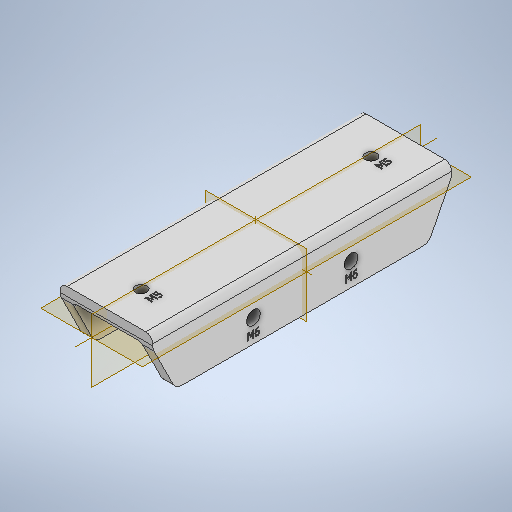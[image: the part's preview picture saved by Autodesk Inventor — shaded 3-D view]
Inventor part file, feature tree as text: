
AUTODESK INVENTOR PART (.ipt)
format: ipt  version: 2025 (Build 290162000, 162)  size: 528,896 bytes
history: native  units: mm
features: sketch x5, chamfer x2, fillet x2, hole x2, emboss x2, extrude x1, mirror x1
ambient origin geometry x8: Origin, YZ Plane, XZ Plane, XY Plane, X Axis, Y Axis, Z Axis, Center Point
bodies: Solid1 (feature_tree)
feature tree (15):
  extrude  "Extrusion1"  Depth=30.2mm
  chamfer  "Chamfer1"  Distance=130.0mm
  chamfer  "Chamfer2"  Distance=10.0mm Angle=60.0deg
  fillet  "Fillet1"  Radius=5.0mm
  hole  "Hole1"  [1 undecoded]
  hole  "Hole2"  [1 undecoded]
  mirror  "Mirror3"
  emboss  "Emboss1"
  emboss  "Emboss2"
  fillet  "Fillet4"  Radius=50.0mm
  sketch  "Sketch1"  dims[d0=20.0mm d1=30.2mm]
  sketch  "Sketch2"  dims[d2=5.0mm]
  sketch  "Sketch3"  dims[d3=2.0mm]
  sketch  "Sketch4"  dims[d4=3.0mm d5=130.0mm d6=0.0mm d7=20.0mm d8=10.0mm d9=60.0deg]
  sketch  "Sketch5"  dims[d10=20.0mm d11=10.0mm d12=60.0deg d13=5.0mm d14=6.0mm d15=6.0mm d16=4.0mm d17=2.0mm d18=90.0deg d19=8.0mm d20=20.594885mm d21=10.0mm d22=21.25mm d23=5.0mm d24=6.0mm d25=4.0mm d26=2.0mm d27=90.0deg d28=8.0mm d29=20.594885mm d30=50.0mm d31=1.5mm d32=0.0mm d33=1.5mm d34=0.0mm d42=4.0mm d41=0.0mm d43=0.0mm d44=0.0mm]
note: 2 required parameter values undecoded (feature->parameter linkage not recoverable at this tier; creation-order binding heuristic only, values carry confidence <= 0.55)
